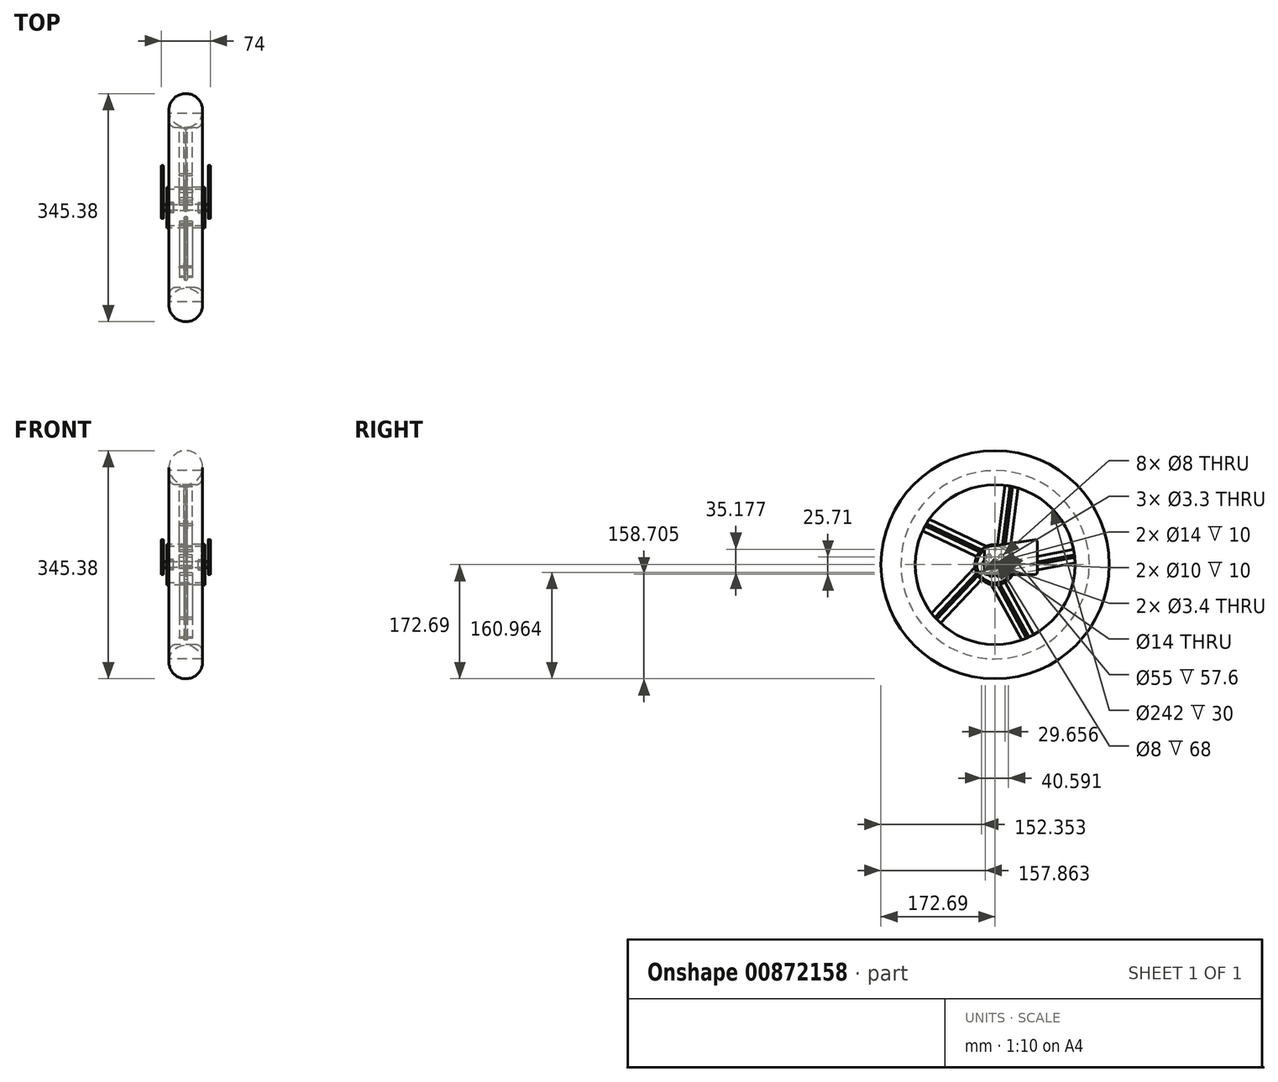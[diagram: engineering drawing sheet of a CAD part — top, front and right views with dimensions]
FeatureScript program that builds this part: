
annotation { "Feature Type Name" : "Feature", "Feature Type Description" : "" }
export const myFeature = defineFeature(function(context is Context, id is Id, definition is map)
    precondition{}
    {
        {
            var Q0;
            Q0=qCreatedBy(makeId("Right.planeOp"),FACE);
            cPlane(context, id + "F0", {"entities" : qUnion([Q0]), "cplaneType" : CPlaneType.OFFSET, "offset" : 34 * mm, "width" : 150 * mm, "height" : 150 * mm});
        }
        {
            var Q0;
            Q0=qCreatedBy(id+"F0.planeOp",FACE);
            cPlane(context, id + "F1", {"entities" : qUnion([Q0]), "cplaneType" : CPlaneType.OFFSET, "offset" : 68 * mm, "oppositeDirection" : true, "width" : 150 * mm, "height" : 150 * mm});
        }
        {
            var Q0;
            Q0=qCreatedBy(id+"F0.planeOp",FACE);
            var sketch = newSketch(context, id + "F2", { "sketchPlane" : qUnion([Q0])});
            skCircle(sketch, "E0", {"center": v(0, 0) * mm, "radius": 4 * mm});
            skLineSegment(sketch, "E1", {"start": v(-16.29, 23.76) * mm, "end": v(-16.29, -11.66) * mm});
            skLineSegment(sketch, "E2", {"start": v(-13.29, -14.66) * mm, "end": v(60.71, -14.66) * mm});
            skLineSegment(sketch, "E3", {"start": v(63.71, -11.66) * mm, "end": v(63.71, 34.86) * mm});
            skLineSegment(sketch, "E4", {"start": v(60.27, 37.82) * mm, "end": v(-13.73, 26.72) * mm});
            skPoint(sketch, "E5.visualSharp", {"position": v(-16.29, 26.34) * mm});
            skArc(sketch, "E5.filletArc", {"start": v(-13.73, 26.72) * mm, "mid": v(-15.56, 25.72) * mm, "end": v(-16.29, 23.76) * mm});
            skPoint(sketch, "E6.visualSharp", {"position": v(-16.29, -14.66) * mm});
            skArc(sketch, "E6.filletArc", {"start": v(-16.29, -11.66) * mm, "mid": v(-15.4, -13.78) * mm, "end": v(-13.29, -14.66) * mm});
            skPoint(sketch, "E7.visualSharp", {"position": v(63.71, -14.66) * mm});
            skArc(sketch, "E7.filletArc", {"start": v(60.71, -14.66) * mm, "mid": v(62.83, -13.78) * mm, "end": v(63.71, -11.66) * mm});
            skPoint(sketch, "E8.visualSharp", {"position": v(63.71, 38.34) * mm});
            skArc(sketch, "E8.filletArc", {"start": v(63.71, 34.86) * mm, "mid": v(62.67, 37.13) * mm, "end": v(60.27, 37.82) * mm});
            skSolve(sketch);
        }
        {
            var Q0;
            Q0=qCreatedBy(id+"F1.planeOp",FACE);
            var sketch = newSketch(context, id + "F3", { "sketchPlane" : qUnion([Q0])});
            skCircle(sketch, "E9", {"center": v(0, 0) * mm, "radius": 4 * mm});
            skLineSegment(sketch, "E10", {"start": v(-7.28, 6.1) * mm, "end": v(-7.28, -3.36) * mm});
            skLineSegment(sketch, "E11", {"start": v(-4.28, -6.36) * mm, "end": v(19.72, -6.36) * mm});
            skLineSegment(sketch, "E12", {"start": v(22.72, -3.36) * mm, "end": v(22.72, 10.1) * mm});
            skLineSegment(sketch, "E13", {"start": v(19.22, 13.06) * mm, "end": v(-4.78, 9.06) * mm});
            skPoint(sketch, "E14.visualSharp", {"position": v(-7.28, 8.64) * mm});
            skArc(sketch, "E14.filletArc", {"start": v(-4.78, 9.06) * mm, "mid": v(-6.57, 8.04) * mm, "end": v(-7.28, 6.1) * mm});
            skPoint(sketch, "E15.visualSharp", {"position": v(-7.28, -6.36) * mm});
            skArc(sketch, "E15.filletArc", {"start": v(-7.28, -3.36) * mm, "mid": v(-6.4, -5.48) * mm, "end": v(-4.28, -6.36) * mm});
            skPoint(sketch, "E16.visualSharp", {"position": v(22.72, -6.36) * mm});
            skArc(sketch, "E16.filletArc", {"start": v(19.72, -6.36) * mm, "mid": v(21.84, -5.48) * mm, "end": v(22.72, -3.36) * mm});
            skPoint(sketch, "E17.visualSharp", {"position": v(22.48, 17.2) * mm});
            skArc(sketch, "E17.filletArc", {"start": v(22.72, 10.1) * mm, "mid": v(21.66, 12.39) * mm, "end": v(19.22, 13.06) * mm});
            skSolve(sketch);
        }
        {
            var Q0;
            Q0=qCreatedBy(makeId("Right.planeOp"),FACE);
            var sketch = newSketch(context, id + "F4", { "sketchPlane" : qUnion([Q0])});
            skCircle(sketch, "E18", {"center": v(0, 0) * mm, "radius": 4 * mm});
            skCircle(sketch, "E19", {"center": v(0, 0) * mm, "radius": 5 * mm});
            skCircle(sketch, "E20", {"center": v(0, 0) * mm, "radius": 1.7 * mm});
            skSolve(sketch);
        }
        {
            var Q0;
            Q0=makeQuery(id+"F2.imprint","IMPRINT",FACE,{"disambiguationData":[TD([[makeQuery(id+"F2.imprint","IMPRINT",EDGE,{"derivedFrom":sQuery(id+"F2.wireOp",EDGE,"E0")}),-1.0]])]});
            extrude(context, id + "F5", {"entities" : qUnion([Q0]), "depth" : 3 * mm, "offsetDistance" : 25 * mm});
        }
        {
            var Q0;
            Q0=makeQuery(id+"F3.imprint","IMPRINT",FACE,{"disambiguationData":[TD([[makeQuery(id+"F3.imprint","IMPRINT",EDGE,{"derivedFrom":sQuery(id+"F3.wireOp",EDGE,"E9")}),-1.0]])]});
            extrude(context, id + "F6", {"entities" : qUnion([Q0]), "oppositeDirection" : true, "depth" : 3 * mm, "offsetDistance" : 25 * mm});
        }
        {
            var Q0;
            Q0=makeQuery(id+"F4.imprint","IMPRINT",FACE,{"disambiguationData":[TD([[makeQuery(id+"F4.imprint","IMPRINT",EDGE,{"derivedFrom":sQuery(id+"F4.wireOp",EDGE,"E18")}),1.0]])]});
            extrude(context, id + "F7", {"entities" : qUnion([Q0]), "endBound" : BoundingType.SYMMETRIC, "depth" : 71 * mm, "offsetDistance" : 25 * mm});
        }
        {
            var Q0;
            Q0=makeQuery(id+"F4.imprint","IMPRINT",FACE,{"disambiguationData":[TD([[makeQuery(id+"F4.imprint","IMPRINT",EDGE,{"derivedFrom":sQuery(id+"F4.wireOp",EDGE,"E18")}),-1.0]])]});
            extrude(context, id + "F8", {"entities" : qUnion([Q0]), "endBound" : BoundingType.SYMMETRIC, "depth" : 68 * mm, "offsetDistance" : 25 * mm});
        }
        {
            var Q0;
            Q0=qCreatedBy(makeId("Right.planeOp"),FACE);
            var sketch = newSketch(context, id + "F9", { "sketchPlane" : qUnion([Q0])});
            skCircle(sketch, "E21", {"center": v(0, 0) * mm, "radius": 30.5 * mm});
            skCircle(sketch, "E22", {"center": v(0, 0) * mm, "radius": 27.5 * mm});
            skCircle(sketch, "E23", {"center": v(0, 0) * mm, "radius": 142.5 * mm});
            skCircle(sketch, "E24", {"center": v(0, 0) * mm, "radius": 121 * mm});
            skLineSegment(sketch, "E25.trimOffspring", {"start": v(13.1, 27.55) * mm, "end": v(24.8, 118.43) * mm, "construction": true});
            skLineSegment(sketch, "E26.1.0", {"start": v(-22.15, 20.96) * mm, "end": v(-104.98, 60.18) * mm, "construction": true});
            skLineSegment(sketch, "E26.2.0", {"start": v(-26.78, -14.6) * mm, "end": v(-89.67, -81.24) * mm, "construction": true});
            skLineSegment(sketch, "E26.3.0", {"start": v(5.6, -29.98) * mm, "end": v(49.56, -110.39) * mm, "construction": true});
            skLineSegment(sketch, "E26.4.0", {"start": v(30.24, -3.94) * mm, "end": v(120.3, 13.02) * mm, "construction": true});
            skLineSegment(sketch, "E27.0", {"start": v(14.94, 26.25) * mm, "end": v(26.75, 118) * mm});
            skLineSegment(sketch, "E28.0", {"start": v(11.18, 28.38) * mm, "end": v(22.83, 118.83) * mm});
            skLineSegment(sketch, "E29.0", {"start": v(22.3, 20.8) * mm, "end": v(34.56, 115.96) * mm});
            skLineSegment(sketch, "E30.0", {"start": v(3.36, 30.31) * mm, "end": v(14.92, 120.08) * mm});
            skLineSegment(sketch, "E31.1.0", {"start": v(-27.8, 12.57) * mm, "end": v(-109.59, 51.3) * mm});
            skLineSegment(sketch, "E31.1.1", {"start": v(-23.53, 19.4) * mm, "end": v(-105.96, 58.43) * mm});
            skLineSegment(sketch, "E31.1.2", {"start": v(-20.35, 22.32) * mm, "end": v(-103.96, 61.9) * mm});
            skLineSegment(sketch, "E31.1.3", {"start": v(-12.9, 27.64) * mm, "end": v(-99.6, 68.7) * mm});
            skLineSegment(sketch, "E31.2.0", {"start": v(-20.54, -22.55) * mm, "end": v(-82.65, -88.37) * mm});
            skLineSegment(sketch, "E31.2.1", {"start": v(-25.72, -16.39) * mm, "end": v(-88.31, -82.72) * mm});
            skLineSegment(sketch, "E31.2.2", {"start": v(-27.52, -12.46) * mm, "end": v(-91, -79.74) * mm});
            skLineSegment(sketch, "E31.2.3", {"start": v(-30.27, -3.72) * mm, "end": v(-96.12, -73.5) * mm});
            skLineSegment(sketch, "E31.3.0", {"start": v(15.1, -26.5) * mm, "end": v(58.5, -105.91) * mm});
            skLineSegment(sketch, "E31.3.1", {"start": v(7.63, -29.53) * mm, "end": v(51.38, -109.55) * mm});
            skLineSegment(sketch, "E31.3.2", {"start": v(3.35, -30.02) * mm, "end": v(47.72, -111.2) * mm});
            skLineSegment(sketch, "E31.3.3", {"start": v(-5.82, -29.94) * mm, "end": v(40.2, -114.13) * mm});
            skLineSegment(sketch, "E31.4.0", {"start": v(29.87, 6.17) * mm, "end": v(118.81, 22.92) * mm});
            skLineSegment(sketch, "E31.4.1", {"start": v(30.44, -1.86) * mm, "end": v(120.07, 15.01) * mm});
            skLineSegment(sketch, "E31.4.2", {"start": v(29.59, -6.1) * mm, "end": v(120.5, 11.02) * mm});
            skLineSegment(sketch, "E31.4.3", {"start": v(26.68, -14.78) * mm, "end": v(120.96, 2.97) * mm});
            skSolve(sketch);
        }
        {
            var Q0;
            Q0=makeQuery(id+"F9.imprint","IMPRINT",FACE,{"disambiguationData":[TD([[makeQuery(id+"F9.imprint","IMPRINT",EDGE,{"derivedFrom":sQuery(id+"F9.wireOp",EDGE,"E21")}),1.0]])]});
            extrude(context, id + "F10", {"entities" : qUnion([Q0]), "endBound" : BoundingType.SYMMETRIC, "depth" : 57.6 * mm, "offsetDistance" : 25 * mm});
        }
        {
            var Q0;
            Q0=makeQuery(id+"F10.opExtrude","CAP_FACE",FACE,{"disambiguationData":[OSD([sQuery(id+"F9.wireOp",EDGE,"E21"),sQuery(id+"F9.wireOp",EDGE,"E22")])],"isStart":false});
            var sketch = newSketch(context, id + "F11", { "sketchPlane" : qUnion([Q0])});
            skCircle(sketch, "E32", {"center": v(0, 0) * mm, "radius": 27.92 * mm});
            skCircle(sketch, "E33", {"center": v(0, 0) * mm, "radius": 7 * mm});
            skCircle(sketch, "E34", {"center": v(0, 0) * mm, "radius": 5 * mm});
            skCircle(sketch, "E35", {"center": v(0, 0) * mm, "radius": 23.45 * mm, "construction": true});
            skCircle(sketch, "E36", {"center": v(0, 23.45) * mm, "radius": 1.65 * mm});
            skCircle(sketch, "E37.1.0", {"center": v(-20.34, -11.68) * mm, "radius": 1.65 * mm});
            skCircle(sketch, "E37.2.0", {"center": v(20.25, -11.73) * mm, "radius": 1.65 * mm});
            skPoint(sketch, "E37.center", {"position": v(-0.03, 0.02) * mm});
            skCircle(sketch, "E38", {"center": v(0, 23.45) * mm, "radius": 15 * mm, "construction": true});
            skCircle(sketch, "E39", {"center": v(-20.34, -11.68) * mm, "radius": 15 * mm, "construction": true});
            skCircle(sketch, "E40", {"center": v(20.25, -11.73) * mm, "radius": 15 * mm, "construction": true});
            skCircle(sketch, "E41", {"center": v(0, 0) * mm, "radius": 15 * mm, "construction": true});
            skCircle(sketch, "E42", {"center": v(-9.35, 11.73) * mm, "radius": 4 * mm});
            skCircle(sketch, "E43", {"center": v(-14.83, 2.27) * mm, "radius": 4 * mm});
            skCircle(sketch, "E44", {"center": v(9.35, 11.73) * mm, "radius": 4 * mm});
            skCircle(sketch, "E45", {"center": v(14.83, 2.26) * mm, "radius": 4 * mm});
            skCircle(sketch, "E46", {"center": v(5.42, -13.98) * mm, "radius": 4 * mm});
            skCircle(sketch, "E47", {"center": v(-5.51, -13.95) * mm, "radius": 4 * mm});
            skSolve(sketch);
        }
        {
            var Q0;
            Q0=makeQuery(id+"F11.imprint","IMPRINT",FACE,{"disambiguationData":[TD([[makeQuery(id+"F11.imprint","IMPRINT",EDGE,{"derivedFrom":sQuery(id+"F11.wireOp",EDGE,"E33")}),-1.0]])]});
            extrude(context, id + "F12", {"entities" : qUnion([Q0]), "oppositeDirection" : true, "depth" : 5 * mm, "offsetDistance" : 25 * mm});
        }
        {
            var Q0;
            Q0=makeQuery(id+"F11.imprint","IMPRINT",FACE,{"disambiguationData":[TD([[makeQuery(id+"F11.imprint","IMPRINT",EDGE,{"derivedFrom":sQuery(id+"F11.wireOp",EDGE,"E33")}),1.0]])]});
            extrude(context, id + "F13", {"entities" : qUnion([Q0]), "oppositeDirection" : true, "depth" : 10 * mm, "offsetDistance" : 25 * mm});
        }
        {
            var Q0;
            Q0=makeQuery(id+"F11.imprint","IMPRINT",FACE,{"disambiguationData":[TD([[makeQuery(id+"F11.imprint","IMPRINT",EDGE,{"derivedFrom":sQuery(id+"F11.wireOp",EDGE,"E33")}),-1.0]])]});
            var sketch = newSketch(context, id + "F14", { "sketchPlane" : qUnion([Q0])});
            skCircle(sketch, "E48", {"center": v(0, 0) * mm, "radius": 7 * mm});
            skCircle(sketch, "E49", {"center": v(0, 0) * mm, "radius": 8 * mm});
            skSolve(sketch);
        }
        {
            var Q0;
            Q0=makeQuery(id+"F14.imprint","IMPRINT",FACE,{"disambiguationData":[TD([[makeQuery(id+"F14.imprint","IMPRINT",EDGE,{"derivedFrom":sQuery(id+"F14.wireOp",EDGE,"E48")}),-1.0]])]});
            extrude(context, id + "F15", {"entities" : qUnion([Q0]), "oppositeDirection" : true, "depth" : 10 * mm, "offsetDistance" : 25 * mm});
        }
        {
            var Q0;
            Q0=makeQuery(id+"F15.opExtrude","SWEPT_BODY",BODY,{"disambiguationData":[OSD([sQuery(id+"F14.wireOp",EDGE,"E48"),sQuery(id+"F14.wireOp",EDGE,"E49")])]});
            var Q1;
            Q1=makeQuery(id+"F13.opExtrude","SWEPT_BODY",BODY,{"disambiguationData":[OSD([sQuery(id+"F11.wireOp",EDGE,"E33"),sQuery(id+"F11.wireOp",EDGE,"E34")])]});
            var Q2;
            Q2=qCreatedBy(makeId("Right.planeOp"),FACE);
            mirror(context, id + "F16", {"entities" : qUnion([Q0, Q1]), "mirrorPlane" : qUnion([Q2])});
        }
        {
            var Q0;
            Q0=qCreatedBy(makeId("Right.planeOp"),FACE);
            var sketch = newSketch(context, id + "F17", { "sketchPlane" : qUnion([Q0])});
            skCircle(sketch, "E50", {"center": v(0, 0) * mm, "radius": 4 * mm});
            skSolve(sketch);
        }
        {
            var Q0;
            Q0 = qSketchRegion(id + "F17", true);
            extrude(context, id + "F18", {"entities" : qUnion([Q0]), "endBound" : BoundingType.SYMMETRIC, "depth" : 51 * mm, "offsetDistance" : 25 * mm});
        }
        {
            var Q0;
            Q0=makeQuery(id+"F18.opExtrude","SWEPT_BODY",BODY,{"disambiguationData":[OSD([sQuery(id+"F17.wireOp",EDGE,"E50")])]});
            var Q1;
            Q1=makeQuery(id+"F7.opExtrude","SWEPT_BODY",BODY,{"disambiguationData":[OSD([sQuery(id+"F4.wireOp",EDGE,"E18"),sQuery(id+"F4.wireOp",EDGE,"E20")])]});
            booleanBodies(context, id + "F19", {"operationType" : BooleanOperationType.SUBTRACTION, "tools" : qUnion([Q0]), "targets" : qUnion([Q1])});
        }
        {
            var Q0;
            Q0=makeQuery(id+"F9.imprint","IMPRINT",FACE,{"disambiguationData":[TD([[makeQuery(id+"F9.imprint","IMPRINT",EDGE,{"derivedFrom":sQuery(id+"F9.wireOp",EDGE,"E23")}),1.0]])]});
            extrude(context, id + "F20", {"entities" : qUnion([Q0]), "endBound" : BoundingType.SYMMETRIC, "depth" : 50 * mm, "offsetDistance" : 25 * mm});
        }
        {
            var Q0;
            Q0=makeQuery(id+"F20.opExtrude","CAP_EDGE",EDGE,{"disambiguationData":[OSD([sQuery(id+"F9.wireOp",EDGE,"E24")])],"isStart":false});
            var Q1;
            Q1=makeQuery(id+"F20.opExtrude","CAP_EDGE",EDGE,{"disambiguationData":[OSD([sQuery(id+"F9.wireOp",EDGE,"E24")])],"isStart":true});
            fillet(context, id + "F21", {"entities" : qUnion([Q0, Q1]), "radius" : 10 * mm, "tangentPropagation" : true, "allowEdgeOverflow" : false});
        }
        {
            var Q0;
            {var subQ0=sQuery(id+"F9.wireOp",EDGE,"E31.3.3");Q0=makeQuery(id+"F9.imprint","IMPRINT",FACE,{"disambiguationData":[TD([[makeQuery(id+"F9.imprint","IMPRINT",EDGE,{"derivedFrom":subQ0}),1.0]])]});}
            var Q1;
            {var subQ0=sQuery(id+"F9.wireOp",EDGE,"E31.3.0");Q1=makeQuery(id+"F9.imprint","IMPRINT",FACE,{"disambiguationData":[TD([[makeQuery(id+"F9.imprint","IMPRINT",EDGE,{"derivedFrom":subQ0}),-1.0]])]});}
            var Q2;
            {var subQ0=sQuery(id+"F9.wireOp",EDGE,"E31.4.3");Q2=makeQuery(id+"F9.imprint","IMPRINT",FACE,{"disambiguationData":[TD([[makeQuery(id+"F9.imprint","IMPRINT",EDGE,{"derivedFrom":subQ0}),1.0]])]});}
            var Q3;
            {var subQ0=sQuery(id+"F9.wireOp",EDGE,"E31.4.0");Q3=makeQuery(id+"F9.imprint","IMPRINT",FACE,{"disambiguationData":[TD([[makeQuery(id+"F9.imprint","IMPRINT",EDGE,{"derivedFrom":subQ0}),-1.0]])]});}
            var Q4;
            {var subQ0=sQuery(id+"F9.wireOp",EDGE,"E29.0");Q4=makeQuery(id+"F9.imprint","IMPRINT",FACE,{"disambiguationData":[TD([[makeQuery(id+"F9.imprint","IMPRINT",EDGE,{"derivedFrom":subQ0}),1.0]])]});}
            var Q5;
            {var subQ0=sQuery(id+"F9.wireOp",EDGE,"E28.0");Q5=makeQuery(id+"F9.imprint","IMPRINT",FACE,{"disambiguationData":[TD([[makeQuery(id+"F9.imprint","IMPRINT",EDGE,{"derivedFrom":subQ0}),1.0]])]});}
            var Q6;
            {var subQ0=sQuery(id+"F9.wireOp",EDGE,"E31.1.3");Q6=makeQuery(id+"F9.imprint","IMPRINT",FACE,{"disambiguationData":[TD([[makeQuery(id+"F9.imprint","IMPRINT",EDGE,{"derivedFrom":subQ0}),1.0]])]});}
            var Q7;
            {var subQ0=sQuery(id+"F9.wireOp",EDGE,"E31.1.0");Q7=makeQuery(id+"F9.imprint","IMPRINT",FACE,{"disambiguationData":[TD([[makeQuery(id+"F9.imprint","IMPRINT",EDGE,{"derivedFrom":subQ0}),-1.0]])]});}
            var Q8;
            {var subQ0=sQuery(id+"F9.wireOp",EDGE,"E31.2.3");Q8=makeQuery(id+"F9.imprint","IMPRINT",FACE,{"disambiguationData":[TD([[makeQuery(id+"F9.imprint","IMPRINT",EDGE,{"derivedFrom":subQ0}),1.0]])]});}
            var Q9;
            {var subQ0=sQuery(id+"F9.wireOp",EDGE,"E31.2.0");Q9=makeQuery(id+"F9.imprint","IMPRINT",FACE,{"disambiguationData":[TD([[makeQuery(id+"F9.imprint","IMPRINT",EDGE,{"derivedFrom":subQ0}),-1.0]])]});}
            extrude(context, id + "F22", {"entities" : qUnion([Q0, Q1, Q2, Q3, Q4, Q5, Q6, Q7, Q8, Q9]), "operationType" : NewBodyOperationType.ADD, "endBound" : BoundingType.SYMMETRIC, "depth" : 5 * mm, "offsetDistance" : 25 * mm});
        }
        {
            var Q0;
            Q0=makeQuery(id+"F22.opExtrude","CAP_EDGE",EDGE,{"disambiguationData":[OSD([sQuery(id+"F9.wireOp",EDGE,"E31.4.3")])],"isStart":true});
            var Q1;
            Q1=makeQuery(id+"F22.opExtrude","CAP_EDGE",EDGE,{"disambiguationData":[OSD([sQuery(id+"F9.wireOp",EDGE,"E31.4.0")])],"isStart":true});
            var Q2;
            Q2=makeQuery(id+"F22.opExtrude","CAP_EDGE",EDGE,{"disambiguationData":[OSD([sQuery(id+"F9.wireOp",EDGE,"E29.0")])],"isStart":true});
            var Q3;
            Q3=makeQuery(id+"F22.opExtrude","CAP_EDGE",EDGE,{"disambiguationData":[OSD([sQuery(id+"F9.wireOp",EDGE,"E30.0")])],"isStart":true});
            var Q4;
            Q4=makeQuery(id+"F22.opExtrude","CAP_EDGE",EDGE,{"disambiguationData":[OSD([sQuery(id+"F9.wireOp",EDGE,"E31.1.3")])],"isStart":true});
            var Q5;
            Q5=makeQuery(id+"F22.opExtrude","CAP_EDGE",EDGE,{"disambiguationData":[OSD([sQuery(id+"F9.wireOp",EDGE,"E31.2.3")])],"isStart":true});
            var Q6;
            Q6=makeQuery(id+"F22.opExtrude","CAP_EDGE",EDGE,{"disambiguationData":[OSD([sQuery(id+"F9.wireOp",EDGE,"E31.3.3")])],"isStart":true});
            var Q7;
            Q7=makeQuery(id+"F22.opExtrude","CAP_EDGE",EDGE,{"disambiguationData":[OSD([sQuery(id+"F9.wireOp",EDGE,"E31.3.0")])],"isStart":true});
            var Q8;
            Q8=makeQuery(id+"F22.opExtrude","CAP_EDGE",EDGE,{"disambiguationData":[OSD([sQuery(id+"F9.wireOp",EDGE,"E31.1.0")])],"isStart":true});
            var Q9;
            Q9=makeQuery(id+"F22.opExtrude","CAP_EDGE",EDGE,{"disambiguationData":[OSD([sQuery(id+"F9.wireOp",EDGE,"E31.2.0")])],"isStart":true});
            var Q10;
            Q10=makeQuery(id+"F22.opExtrude","CAP_EDGE",EDGE,{"disambiguationData":[OSD([sQuery(id+"F9.wireOp",EDGE,"E31.4.3")])],"isStart":false});
            var Q11;
            Q11=makeQuery(id+"F22.opExtrude","CAP_EDGE",EDGE,{"disambiguationData":[OSD([sQuery(id+"F9.wireOp",EDGE,"E31.4.0")])],"isStart":false});
            var Q12;
            Q12=makeQuery(id+"F22.opExtrude","CAP_EDGE",EDGE,{"disambiguationData":[OSD([sQuery(id+"F9.wireOp",EDGE,"E31.3.0")])],"isStart":false});
            var Q13;
            Q13=makeQuery(id+"F22.opExtrude","CAP_EDGE",EDGE,{"disambiguationData":[OSD([sQuery(id+"F9.wireOp",EDGE,"E31.3.3")])],"isStart":false});
            var Q14;
            Q14=makeQuery(id+"F22.opExtrude","CAP_EDGE",EDGE,{"disambiguationData":[OSD([sQuery(id+"F9.wireOp",EDGE,"E31.2.0")])],"isStart":false});
            var Q15;
            Q15=makeQuery(id+"F22.opExtrude","CAP_EDGE",EDGE,{"disambiguationData":[OSD([sQuery(id+"F9.wireOp",EDGE,"E31.2.3")])],"isStart":false});
            var Q16;
            Q16=makeQuery(id+"F22.opExtrude","CAP_EDGE",EDGE,{"disambiguationData":[OSD([sQuery(id+"F9.wireOp",EDGE,"E31.1.0")])],"isStart":false});
            var Q17;
            Q17=makeQuery(id+"F22.opExtrude","CAP_EDGE",EDGE,{"disambiguationData":[OSD([sQuery(id+"F9.wireOp",EDGE,"E31.1.3")])],"isStart":false});
            var Q18;
            Q18=makeQuery(id+"F22.opExtrude","CAP_EDGE",EDGE,{"disambiguationData":[OSD([sQuery(id+"F9.wireOp",EDGE,"E29.0")])],"isStart":false});
            var Q19;
            Q19=makeQuery(id+"F22.opExtrude","CAP_EDGE",EDGE,{"disambiguationData":[OSD([sQuery(id+"F9.wireOp",EDGE,"E30.0")])],"isStart":false});
            fillet(context, id + "F23", {"entities" : qUnion([Q0, Q1, Q2, Q3, Q4, Q5, Q6, Q7, Q8, Q9, Q10, Q11, Q12, Q13, Q14, Q15, Q16, Q17, Q18, Q19]), "radius" : 3 * mm, "tangentPropagation" : true, "allowEdgeOverflow" : false});
        }
        {
            var Q0;
            {var subQ0=sQuery(id+"F9.wireOp",EDGE,"E28.0");Q0=makeQuery(id+"F9.imprint","IMPRINT",FACE,{"disambiguationData":[TD([[makeQuery(id+"F9.imprint","IMPRINT",EDGE,{"derivedFrom":subQ0}),-1.0]])]});}
            var Q1;
            {var subQ0=sQuery(id+"F9.wireOp",EDGE,"E31.4.1");Q1=makeQuery(id+"F9.imprint","IMPRINT",FACE,{"disambiguationData":[TD([[makeQuery(id+"F9.imprint","IMPRINT",EDGE,{"derivedFrom":subQ0}),-1.0]])]});}
            var Q2;
            {var subQ0=sQuery(id+"F9.wireOp",EDGE,"E31.3.1");Q2=makeQuery(id+"F9.imprint","IMPRINT",FACE,{"disambiguationData":[TD([[makeQuery(id+"F9.imprint","IMPRINT",EDGE,{"derivedFrom":subQ0}),-1.0]])]});}
            var Q3;
            {var subQ0=sQuery(id+"F9.wireOp",EDGE,"E31.2.1");Q3=makeQuery(id+"F9.imprint","IMPRINT",FACE,{"disambiguationData":[TD([[makeQuery(id+"F9.imprint","IMPRINT",EDGE,{"derivedFrom":subQ0}),-1.0]])]});}
            var Q4;
            {var subQ0=sQuery(id+"F9.wireOp",EDGE,"E31.1.1");Q4=makeQuery(id+"F9.imprint","IMPRINT",FACE,{"disambiguationData":[TD([[makeQuery(id+"F9.imprint","IMPRINT",EDGE,{"derivedFrom":subQ0}),-1.0]])]});}
            extrude(context, id + "F24", {"entities" : qUnion([Q0, Q1, Q2, Q3, Q4]), "operationType" : NewBodyOperationType.ADD, "endBound" : BoundingType.SYMMETRIC, "depth" : 20 * mm, "offsetDistance" : 25 * mm});
        }
        {
            var Q0;
            Q0=qCreatedBy(makeId("Front.planeOp"),FACE);
            var sketch = newSketch(context, id + "F25", { "sketchPlane" : qUnion([Q0])});
            skLineSegment(sketch, "E51", {"start": v(-68.59, 0) * mm, "end": v(65.79, 0) * mm, "construction": true});
            skCircle(sketch, "E52", {"center": v(0, 147.19) * mm, "radius": 25.5 * mm});
            skSolve(sketch);
        }
        {
            var Q0;
            Q0=makeQuery(id+"F25.imprint","IMPRINT",FACE,{"disambiguationData":[TD([[makeQuery(id+"F25.imprint","IMPRINT",EDGE,{"derivedFrom":sQuery(id+"F25.wireOp",EDGE,"E52")}),1.0]])]});
            var Q1;
            Q1=sQuery(id+"F25.wireOp",EDGE,"E51");
            revolve(context, id + "F26", {"surfaceOperationType" : NewSurfaceOperationType.NEW, "entities" : qUnion([Q0]), "axis" : qUnion([Q1]), "revolveType" : RevolveType.FULL});
        }
        {
            var Q0;
            Q0=makeQuery(id+"F6.opExtrude","SWEPT_BODY",BODY,{"disambiguationData":[OSD([sQuery(id+"F3.wireOp",EDGE,"E9"),sQuery(id+"F3.wireOp",EDGE,"E10"),sQuery(id+"F3.wireOp",EDGE,"E11"),sQuery(id+"F3.wireOp",EDGE,"E12"),sQuery(id+"F3.wireOp",EDGE,"E13"),sQuery(id+"F3.wireOp",EDGE,"E14.filletArc"),sQuery(id+"F3.wireOp",EDGE,"E15.filletArc"),sQuery(id+"F3.wireOp",EDGE,"E16.filletArc"),sQuery(id+"F3.wireOp",EDGE,"E17.filletArc")])]});
            deleteBodies(context, id + "F27", {"entities" : qUnion([Q0])});
        }
        {
            var Q0;
            Q0=makeQuery(id+"F5.opExtrude","SWEPT_BODY",BODY,{"disambiguationData":[OSD([sQuery(id+"F2.wireOp",EDGE,"E0"),sQuery(id+"F2.wireOp",EDGE,"E1"),sQuery(id+"F2.wireOp",EDGE,"E2"),sQuery(id+"F2.wireOp",EDGE,"E3"),sQuery(id+"F2.wireOp",EDGE,"E4"),sQuery(id+"F2.wireOp",EDGE,"E5.filletArc"),sQuery(id+"F2.wireOp",EDGE,"E6.filletArc"),sQuery(id+"F2.wireOp",EDGE,"E7.filletArc"),sQuery(id+"F2.wireOp",EDGE,"E8.filletArc")])]});
            var Q1;
            Q1=qCreatedBy(makeId("Right.planeOp"),FACE);
            mirror(context, id + "F28", {"entities" : qUnion([Q0]), "mirrorPlane" : qUnion([Q1])});
        }
    });
